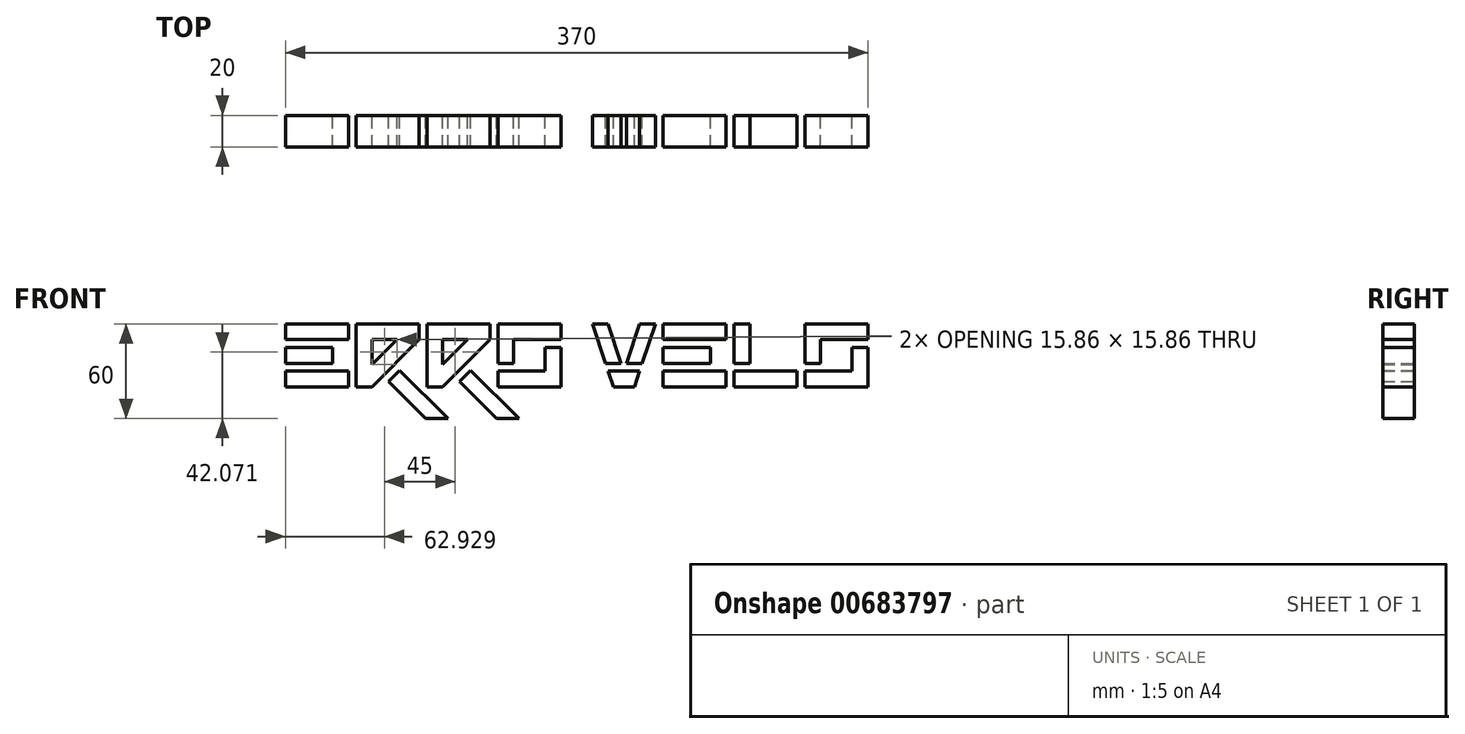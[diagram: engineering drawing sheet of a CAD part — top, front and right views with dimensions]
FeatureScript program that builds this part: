
annotation { "Feature Type Name" : "Feature", "Feature Type Description" : "" }
export const myFeature = defineFeature(function(context is Context, id is Id, definition is map)
    precondition{}
    {
        {
            var Q0;
            Q0=qCreatedBy(makeId("Front.planeOp"),FACE);
            var sketch = newSketch(context, id + "F0", { "sketchPlane" : qUnion([Q0])});
            skLineSegment(sketch, "E0.bottom", {"start": v(0, 0) * mm, "end": v(-40, 0) * mm});
            skLineSegment(sketch, "E0.top", {"start": v(0, 10) * mm, "end": v(-40, 10) * mm});
            skLineSegment(sketch, "E0.left", {"start": v(0, 0) * mm, "end": v(0, 10) * mm});
            skLineSegment(sketch, "E0.right", {"start": v(-40, 0) * mm, "end": v(-40, 10) * mm});
            skLineSegment(sketch, "E1.bottom", {"start": v(-40, 25) * mm, "end": v(-10, 25) * mm});
            skLineSegment(sketch, "E1.top", {"start": v(-40, 15) * mm, "end": v(-10, 15) * mm});
            skLineSegment(sketch, "E1.left", {"start": v(-40, 25) * mm, "end": v(-40, 15) * mm});
            skLineSegment(sketch, "E1.right", {"start": v(-10, 25) * mm, "end": v(-10, 15) * mm});
            skLineSegment(sketch, "E2.bottom", {"start": v(-40, 30) * mm, "end": v(0, 30) * mm});
            skLineSegment(sketch, "E2.top", {"start": v(-40, 40) * mm, "end": v(0, 40) * mm});
            skLineSegment(sketch, "E2.left", {"start": v(-40, 30) * mm, "end": v(-40, 40) * mm});
            skLineSegment(sketch, "E2.right", {"start": v(0, 30) * mm, "end": v(0, 40) * mm});
            skLineSegment(sketch, "E3", {"start": v(5, 0) * mm, "end": v(5, 40) * mm});
            skLineSegment(sketch, "E4", {"start": v(5, 40) * mm, "end": v(45, 40) * mm});
            skLineSegment(sketch, "E5", {"start": v(45, 40) * mm, "end": v(45, 30) * mm});
            skLineSegment(sketch, "E6", {"start": v(15, 0) * mm, "end": v(5, 0) * mm});
            skLineSegment(sketch, "E7", {"start": v(45, 30) * mm, "end": v(29.14, 14.14) * mm});
            skLineSegment(sketch, "E8", {"start": v(15, 0) * mm, "end": v(15, 0) * mm});
            skLineSegment(sketch, "E9", {"start": v(15, 30) * mm, "end": v(30.86, 30) * mm});
            skLineSegment(sketch, "E10", {"start": v(30.86, 30) * mm, "end": v(15, 14.14) * mm});
            skLineSegment(sketch, "E11", {"start": v(15, 14.14) * mm, "end": v(15, 30) * mm});
            skLineSegment(sketch, "E12", {"start": v(25.6, 3.54) * mm, "end": v(49.14, -20) * mm});
            skLineSegment(sketch, "E13", {"start": v(49.14, -20) * mm, "end": v(63.28, -20) * mm});
            skLineSegment(sketch, "E14", {"start": v(63.28, -20) * mm, "end": v(32.68, 10.6) * mm});
            skLineSegment(sketch, "E15", {"start": v(15, 14.14) * mm, "end": v(22.07, 7.07) * mm, "construction": true});
            skLineSegment(sketch, "E16.trimOffspring", {"start": v(22.07, 7.07) * mm, "end": v(15, 0) * mm});
            skLineSegment(sketch, "E17", {"start": v(50, 0) * mm, "end": v(50, 40) * mm});
            skLineSegment(sketch, "E18", {"start": v(50, 40) * mm, "end": v(90, 40) * mm});
            skLineSegment(sketch, "E19", {"start": v(90, 40) * mm, "end": v(90, 30) * mm});
            skLineSegment(sketch, "E20", {"start": v(60, 0) * mm, "end": v(50, 0) * mm});
            skLineSegment(sketch, "E21", {"start": v(90, 30) * mm, "end": v(74.14, 14.14) * mm});
            skLineSegment(sketch, "E22", {"start": v(60, 30) * mm, "end": v(75.86, 30) * mm});
            skLineSegment(sketch, "E23", {"start": v(75.86, 30) * mm, "end": v(60, 14.14) * mm});
            skLineSegment(sketch, "E24", {"start": v(60, 14.14) * mm, "end": v(60, 30) * mm});
            skLineSegment(sketch, "E25", {"start": v(70.6, 3.54) * mm, "end": v(94.14, -20) * mm});
            skLineSegment(sketch, "E26", {"start": v(94.14, -20) * mm, "end": v(108.28, -20) * mm});
            skLineSegment(sketch, "E27", {"start": v(108.28, -20) * mm, "end": v(77.68, 10.6) * mm});
            skLineSegment(sketch, "E28", {"start": v(60, 14.14) * mm, "end": v(67.07, 7.07) * mm, "construction": true});
            skLineSegment(sketch, "E29.trimOffspring", {"start": v(67.07, 7.07) * mm, "end": v(60, 0) * mm});
            skLineSegment(sketch, "E30.bottom", {"start": v(95, 0) * mm, "end": v(135, 0) * mm});
            skLineSegment(sketch, "E30.top", {"start": v(95, 40) * mm, "end": v(135, 40) * mm});
            skLineSegment(sketch, "E30.left", {"start": v(95, 0) * mm, "end": v(95, 10) * mm});
            skLineSegment(sketch, "E30.right", {"start": v(135, 0) * mm, "end": v(135, 25) * mm});
            skLineSegment(sketch, "E31.bottom", {"start": v(105, 30) * mm, "end": v(125, 30) * mm});
            skLineSegment(sketch, "E31.top", {"start": v(105, 10) * mm, "end": v(125, 10) * mm});
            skLineSegment(sketch, "E31.left", {"start": v(105, 30) * mm, "end": v(105, 15) * mm});
            skLineSegment(sketch, "E31.right", {"start": v(125, 30) * mm, "end": v(125, 30) * mm});
            skLineSegment(sketch, "E32", {"start": v(95, 10) * mm, "end": v(105, 10) * mm});
            skLineSegment(sketch, "E33", {"start": v(105, 15) * mm, "end": v(95, 15) * mm});
            skLineSegment(sketch, "E34", {"start": v(125, 30) * mm, "end": v(135, 30) * mm});
            skLineSegment(sketch, "E35", {"start": v(125, 25) * mm, "end": v(135, 25) * mm});
            skLineSegment(sketch, "E36.trimOffspring", {"start": v(95, 15) * mm, "end": v(95, 40) * mm});
            skLineSegment(sketch, "E37.trimOffspring", {"start": v(105, 10) * mm, "end": v(105, 10) * mm});
            skLineSegment(sketch, "E38.trimOffspring", {"start": v(125, 25) * mm, "end": v(125, 10) * mm});
            skLineSegment(sketch, "E39.trimOffspring", {"start": v(135, 30) * mm, "end": v(135, 40) * mm});
            skLineSegment(sketch, "E40", {"start": v(155, 40) * mm, "end": v(163.33, 15) * mm});
            skLineSegment(sketch, "E41", {"start": v(168.33, 0) * mm, "end": v(181.67, 0) * mm});
            skLineSegment(sketch, "E42", {"start": v(181.67, 0) * mm, "end": v(185, 10) * mm});
            skLineSegment(sketch, "E43", {"start": v(195, 40) * mm, "end": v(185, 40) * mm});
            skLineSegment(sketch, "E44", {"start": v(185, 40) * mm, "end": v(176.67, 15) * mm});
            skLineSegment(sketch, "E45", {"start": v(173.33, 15) * mm, "end": v(165, 40) * mm});
            skLineSegment(sketch, "E46", {"start": v(165, 40) * mm, "end": v(155, 40) * mm});
            skLineSegment(sketch, "E47.bottom", {"start": v(240, 0) * mm, "end": v(200, 0) * mm});
            skLineSegment(sketch, "E47.top", {"start": v(240, 10) * mm, "end": v(200, 10) * mm});
            skLineSegment(sketch, "E47.left", {"start": v(240, 0) * mm, "end": v(240, 10) * mm});
            skLineSegment(sketch, "E47.right", {"start": v(200, 0) * mm, "end": v(200, 10) * mm});
            skLineSegment(sketch, "E48.bottom", {"start": v(200, 25) * mm, "end": v(230, 25) * mm});
            skLineSegment(sketch, "E48.top", {"start": v(200, 15) * mm, "end": v(230, 15) * mm});
            skLineSegment(sketch, "E48.left", {"start": v(200, 25) * mm, "end": v(200, 15) * mm});
            skLineSegment(sketch, "E48.right", {"start": v(230, 25) * mm, "end": v(230, 15) * mm});
            skLineSegment(sketch, "E49.bottom", {"start": v(200, 30) * mm, "end": v(240, 30) * mm});
            skLineSegment(sketch, "E49.top", {"start": v(200, 40) * mm, "end": v(240, 40) * mm});
            skLineSegment(sketch, "E49.left", {"start": v(200, 30) * mm, "end": v(200, 40) * mm});
            skLineSegment(sketch, "E49.right", {"start": v(240, 30) * mm, "end": v(240, 40) * mm});
            skLineSegment(sketch, "E50", {"start": v(245, 40) * mm, "end": v(245, 15) * mm});
            skLineSegment(sketch, "E51", {"start": v(245, 0) * mm, "end": v(285, 0) * mm});
            skLineSegment(sketch, "E52", {"start": v(285, 0) * mm, "end": v(285, 10) * mm});
            skLineSegment(sketch, "E53", {"start": v(285, 10) * mm, "end": v(255, 10) * mm});
            skLineSegment(sketch, "E54", {"start": v(255, 15) * mm, "end": v(255, 40) * mm});
            skLineSegment(sketch, "E55", {"start": v(255, 40) * mm, "end": v(245, 40) * mm});
            skLineSegment(sketch, "E56.bottom", {"start": v(290, 0) * mm, "end": v(330, 0) * mm});
            skLineSegment(sketch, "E56.top", {"start": v(290, 40) * mm, "end": v(330, 40) * mm});
            skLineSegment(sketch, "E56.left", {"start": v(290, 0) * mm, "end": v(290, 10) * mm});
            skLineSegment(sketch, "E56.right", {"start": v(330, 0) * mm, "end": v(330, 25) * mm});
            skLineSegment(sketch, "E57.bottom", {"start": v(300, 30) * mm, "end": v(320, 30) * mm});
            skLineSegment(sketch, "E57.top", {"start": v(300, 10) * mm, "end": v(320, 10) * mm});
            skLineSegment(sketch, "E57.left", {"start": v(300, 30) * mm, "end": v(300, 15) * mm});
            skLineSegment(sketch, "E57.right", {"start": v(320, 30) * mm, "end": v(320, 30) * mm});
            skLineSegment(sketch, "E58", {"start": v(290, 10) * mm, "end": v(300, 10) * mm});
            skLineSegment(sketch, "E59", {"start": v(300, 15) * mm, "end": v(290, 15) * mm});
            skLineSegment(sketch, "E60", {"start": v(320, 30) * mm, "end": v(330, 30) * mm});
            skLineSegment(sketch, "E61", {"start": v(320, 25) * mm, "end": v(330, 25) * mm});
            skLineSegment(sketch, "E62.trimOffspring", {"start": v(290, 15) * mm, "end": v(290, 40) * mm});
            skLineSegment(sketch, "E63.trimOffspring", {"start": v(300, 10) * mm, "end": v(300, 10) * mm});
            skLineSegment(sketch, "E64.trimOffspring", {"start": v(320, 25) * mm, "end": v(320, 10) * mm});
            skLineSegment(sketch, "E65.trimOffspring", {"start": v(330, 30) * mm, "end": v(330, 40) * mm});
            skLineSegment(sketch, "E66", {"start": v(185, 10) * mm, "end": v(165, 10) * mm});
            skLineSegment(sketch, "E67", {"start": v(163.33, 15) * mm, "end": v(173.33, 15) * mm});
            skLineSegment(sketch, "E68.trimOffspring", {"start": v(176.67, 15) * mm, "end": v(186.67, 15) * mm});
            skLineSegment(sketch, "E69.trimOffspring", {"start": v(165, 10) * mm, "end": v(168.33, 0) * mm});
            skLineSegment(sketch, "E70.trimOffspring", {"start": v(186.67, 15) * mm, "end": v(195, 40) * mm});
            skPoint(sketch, "E71.orphan", {"position": v(175, 10) * mm});
            skLineSegment(sketch, "E72", {"start": v(255, 10) * mm, "end": v(245, 10) * mm});
            skLineSegment(sketch, "E73", {"start": v(245, 15) * mm, "end": v(255, 15) * mm});
            skLineSegment(sketch, "E74.trimOffspring", {"start": v(245, 10) * mm, "end": v(245, 0) * mm});
            skLineSegment(sketch, "E75", {"start": v(25.6, 3.54) * mm, "end": v(32.68, 10.6) * mm});
            skLineSegment(sketch, "E76", {"start": v(70.6, 3.54) * mm, "end": v(77.68, 10.6) * mm});
            skLineSegment(sketch, "E77", {"start": v(22.07, 7.07) * mm, "end": v(29.14, 14.14) * mm});
            skLineSegment(sketch, "E78", {"start": v(67.07, 7.07) * mm, "end": v(74.14, 14.14) * mm});
            skSolve(sketch);
        }
        {
            var Q0;
            Q0=makeQuery(id+"F0.imprint","IMPRINT",FACE,{"disambiguationData":[TD([[makeQuery(id+"F0.imprint","IMPRINT",EDGE,{"derivedFrom":sQuery(id+"F0.wireOp",EDGE,"E2.bottom")}),1.0]])]});
            var Q1;
            Q1=makeQuery(id+"F0.imprint","IMPRINT",FACE,{"disambiguationData":[TD([[makeQuery(id+"F0.imprint","IMPRINT",EDGE,{"derivedFrom":sQuery(id+"F0.wireOp",EDGE,"E1.bottom")}),-1.0]])]});
            var Q2;
            Q2=makeQuery(id+"F0.imprint","IMPRINT",FACE,{"disambiguationData":[TD([[makeQuery(id+"F0.imprint","IMPRINT",EDGE,{"derivedFrom":sQuery(id+"F0.wireOp",EDGE,"E0.bottom")}),-1.0]])]});
            var Q3;
            Q3=makeQuery(id+"F0.imprint","IMPRINT",FACE,{"disambiguationData":[TD([[makeQuery(id+"F0.imprint","IMPRINT",EDGE,{"derivedFrom":sQuery(id+"F0.wireOp",EDGE,"E3")}),-1.0]])]});
            var Q4;
            Q4=makeQuery(id+"F0.imprint","IMPRINT",FACE,{"disambiguationData":[TD([[makeQuery(id+"F0.imprint","IMPRINT",EDGE,{"derivedFrom":sQuery(id+"F0.wireOp",EDGE,"E17")}),-1.0]])]});
            var Q5;
            Q5=makeQuery(id+"F0.imprint","IMPRINT",FACE,{"disambiguationData":[TD([[makeQuery(id+"F0.imprint","IMPRINT",EDGE,{"derivedFrom":sQuery(id+"F0.wireOp",EDGE,"E30.top")}),-1.0]])]});
            var Q6;
            Q6=makeQuery(id+"F0.imprint","IMPRINT",FACE,{"disambiguationData":[TD([[makeQuery(id+"F0.imprint","IMPRINT",EDGE,{"derivedFrom":sQuery(id+"F0.wireOp",EDGE,"E30.bottom")}),1.0]])]});
            var Q7;
            Q7=makeQuery(id+"F0.imprint","IMPRINT",FACE,{"disambiguationData":[TD([[makeQuery(id+"F0.imprint","IMPRINT",EDGE,{"derivedFrom":sQuery(id+"F0.wireOp",EDGE,"E40")}),1.0]])]});
            var Q8;
            Q8=makeQuery(id+"F0.imprint","IMPRINT",FACE,{"disambiguationData":[TD([[makeQuery(id+"F0.imprint","IMPRINT",EDGE,{"derivedFrom":sQuery(id+"F0.wireOp",EDGE,"E49.bottom")}),1.0]])]});
            var Q9;
            Q9=makeQuery(id+"F0.imprint","IMPRINT",FACE,{"disambiguationData":[TD([[makeQuery(id+"F0.imprint","IMPRINT",EDGE,{"derivedFrom":sQuery(id+"F0.wireOp",EDGE,"E48.bottom")}),-1.0]])]});
            var Q10;
            Q10=makeQuery(id+"F0.imprint","IMPRINT",FACE,{"disambiguationData":[TD([[makeQuery(id+"F0.imprint","IMPRINT",EDGE,{"derivedFrom":sQuery(id+"F0.wireOp",EDGE,"E47.bottom")}),-1.0]])]});
            var Q11;
            Q11=makeQuery(id+"F0.imprint","IMPRINT",FACE,{"disambiguationData":[TD([[makeQuery(id+"F0.imprint","IMPRINT",EDGE,{"derivedFrom":sQuery(id+"F0.wireOp",EDGE,"E50")}),1.0]])]});
            var Q12;
            Q12=makeQuery(id+"F0.imprint","IMPRINT",FACE,{"disambiguationData":[TD([[makeQuery(id+"F0.imprint","IMPRINT",EDGE,{"derivedFrom":sQuery(id+"F0.wireOp",EDGE,"E56.top")}),-1.0]])]});
            var Q13;
            Q13=makeQuery(id+"F0.imprint","IMPRINT",FACE,{"disambiguationData":[TD([[makeQuery(id+"F0.imprint","IMPRINT",EDGE,{"derivedFrom":sQuery(id+"F0.wireOp",EDGE,"E56.bottom")}),1.0]])]});
            var Q14;
            Q14=makeQuery(id+"F0.imprint","IMPRINT",FACE,{"disambiguationData":[TD([[makeQuery(id+"F0.imprint","IMPRINT",EDGE,{"derivedFrom":sQuery(id+"F0.wireOp",EDGE,"E43")}),1.0]])]});
            var Q15;
            Q15=makeQuery(id+"F0.imprint","IMPRINT",FACE,{"disambiguationData":[TD([[makeQuery(id+"F0.imprint","IMPRINT",EDGE,{"derivedFrom":sQuery(id+"F0.wireOp",EDGE,"E41")}),1.0]])]});
            var Q16;
            Q16=makeQuery(id+"F0.imprint","IMPRINT",FACE,{"disambiguationData":[TD([[makeQuery(id+"F0.imprint","IMPRINT",EDGE,{"derivedFrom":sQuery(id+"F0.wireOp",EDGE,"E51")}),1.0]])]});
            var Q17;
            Q17=makeQuery(id+"F0.imprint","IMPRINT",FACE,{"disambiguationData":[TD([[makeQuery(id+"F0.imprint","IMPRINT",EDGE,{"derivedFrom":sQuery(id+"F0.wireOp",EDGE,"E12")}),1.0]])]});
            var Q18;
            Q18=makeQuery(id+"F0.imprint","IMPRINT",FACE,{"disambiguationData":[TD([[makeQuery(id+"F0.imprint","IMPRINT",EDGE,{"derivedFrom":sQuery(id+"F0.wireOp",EDGE,"E25")}),1.0]])]});
            extrude(context, id + "F1", {"entities" : qUnion([Q0, Q1, Q2, Q3, Q4, Q5, Q6, Q7, Q8, Q9, Q10, Q11, Q12, Q13, Q14, Q15, Q16, Q17, Q18]), "depth" : 20 * mm, "offsetDistance" : 25 * mm});
        }
    });
